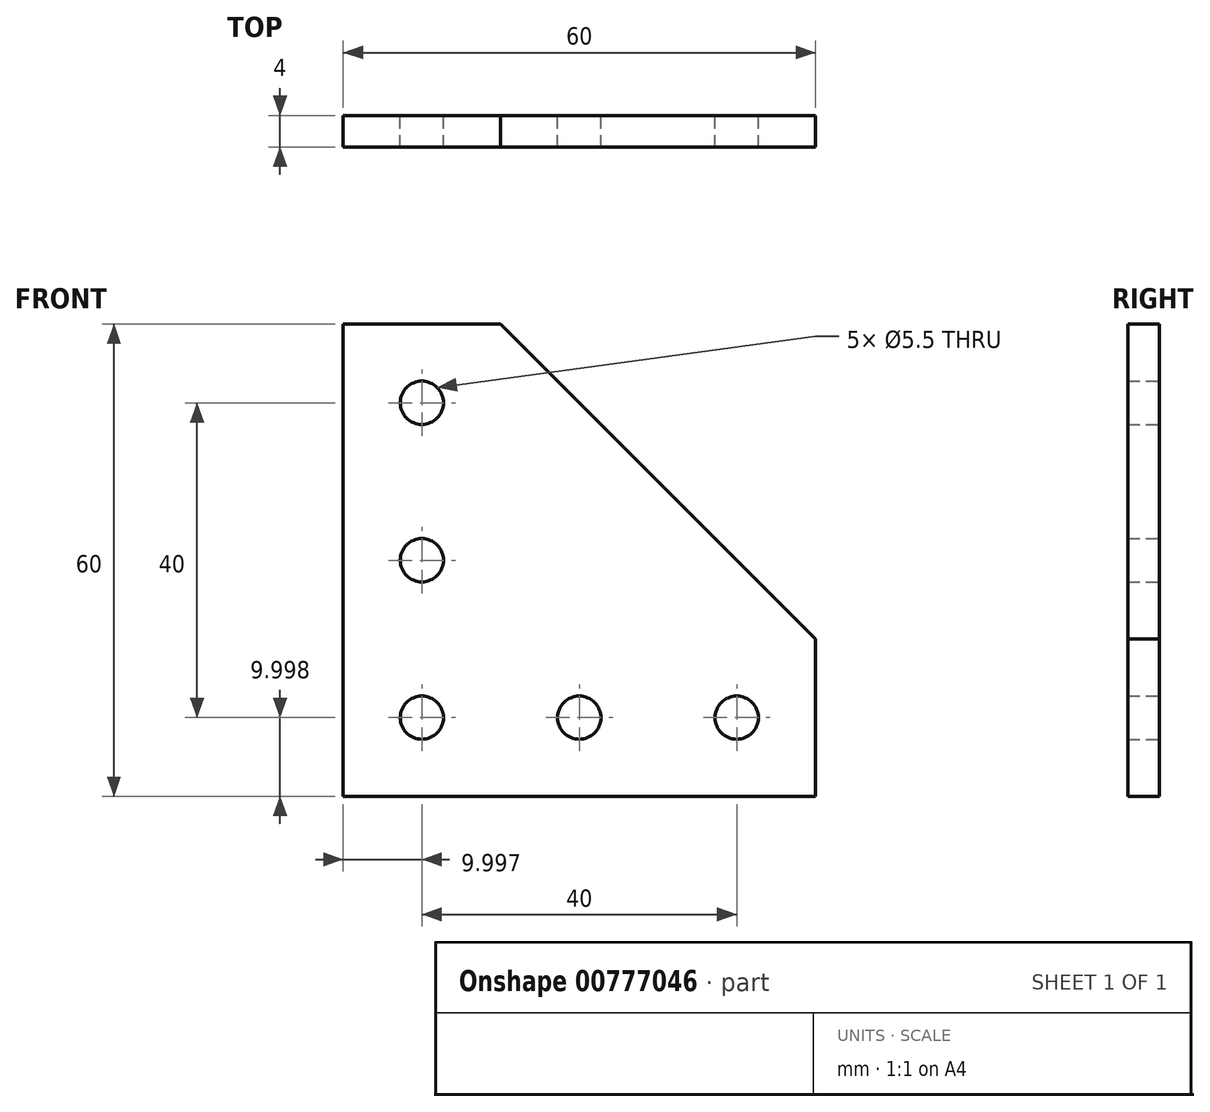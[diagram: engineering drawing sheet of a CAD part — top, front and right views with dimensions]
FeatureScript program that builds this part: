
annotation { "Feature Type Name" : "Feature", "Feature Type Description" : "" }
export const myFeature = defineFeature(function(context is Context, id is Id, definition is map)
    precondition{}
    {
        {
            var Q0;
            Q0=qCreatedBy(makeId("Front.planeOp"),FACE);
            var sketch = newSketch(context, id + "F0", { "sketchPlane" : qUnion([Q0])});
            skLineSegment(sketch, "E0", {"start": v(-35.55, 34.2) * mm, "end": v(-35.55, -25.8) * mm});
            skLineSegment(sketch, "E1", {"start": v(-35.55, -25.8) * mm, "end": v(24.45, -25.8) * mm});
            skLineSegment(sketch, "E2", {"start": v(24.45, -25.8) * mm, "end": v(24.45, -5.8) * mm});
            skLineSegment(sketch, "E3", {"start": v(24.45, -5.8) * mm, "end": v(-15.55, 34.2) * mm});
            skLineSegment(sketch, "E4", {"start": v(-15.55, 34.2) * mm, "end": v(-35.55, 34.2) * mm});
            skCircle(sketch, "E5", {"center": v(-25.55, 24.2) * mm, "radius": 2.75 * mm});
            skPoint(sketch, "E5.centerSnap0", {"position": v(-25.55, 34.2) * mm});
            skCircle(sketch, "E6", {"center": v(-25.55, 4.2) * mm, "radius": 2.75 * mm});
            skCircle(sketch, "E7", {"center": v(-25.55, -15.8) * mm, "radius": 2.75 * mm});
            skPoint(sketch, "E7.centerSnap0", {"position": v(24.45, -15.8) * mm});
            skCircle(sketch, "E8", {"center": v(-5.55, -15.8) * mm, "radius": 2.75 * mm});
            skCircle(sketch, "E9", {"center": v(14.45, -15.8) * mm, "radius": 2.75 * mm});
            skSolve(sketch);
        }
        {
            var Q0;
            Q0=qSketchRegion(id+"F0",true);
            extrude(context, id + "F1", {"entities" : qUnion([Q0]), "depth" : 4 * mm});
        }
    });
